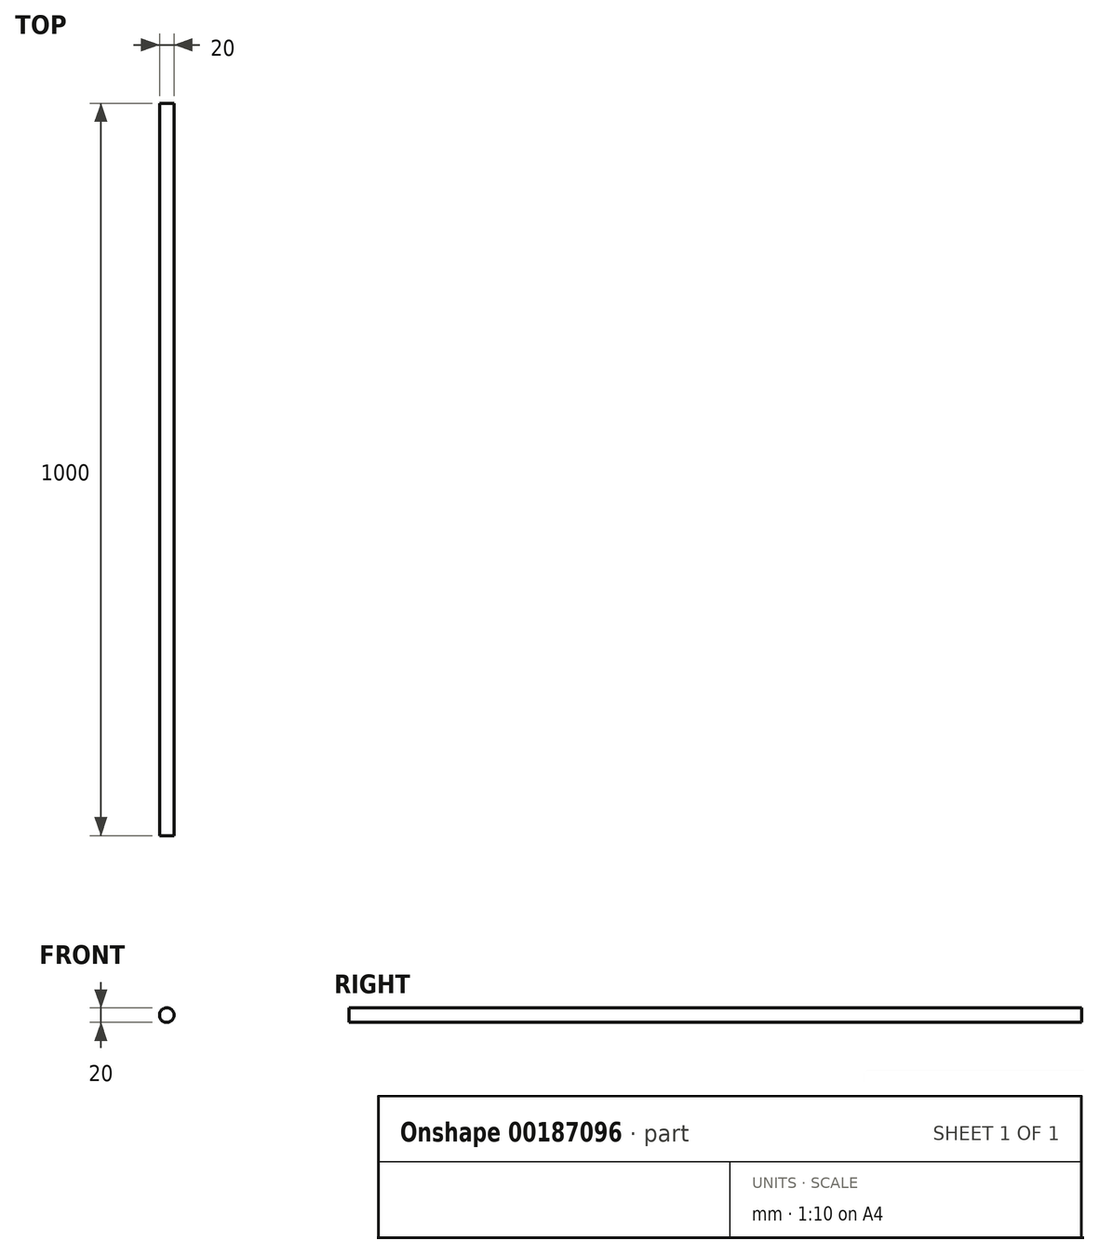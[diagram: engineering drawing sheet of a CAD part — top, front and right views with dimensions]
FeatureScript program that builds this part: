
annotation { "Feature Type Name" : "Feature", "Feature Type Description" : "" }
export const myFeature = defineFeature(function(context is Context, id is Id, definition is map)
    precondition{}
    {
        {
            var Q0;
            Q0=qCreatedBy(makeId("Front.planeOp"),FACE);
            var sketch = newSketch(context, id + "F0", { "sketchPlane" : qUnion([Q0])});
            skCircle(sketch, "E0", {"center": v(0, 0) * mm, "radius": 10 * mm});
            skSolve(sketch);
        }
        {
            var Q0;
            Q0=makeQuery(id+"F0.imprint","IMPRINT",FACE,{"disambiguationData":[TD([[makeQuery(id+"F0.imprint","IMPRINT",EDGE,{"derivedFrom":sQuery(id+"F0.wireOp",EDGE,"E0")}),1.0]])]});
            extrude(context, id + "F1", {"entities" : qUnion([Q0]), "depth" : 1000 * mm});
        }
    });
